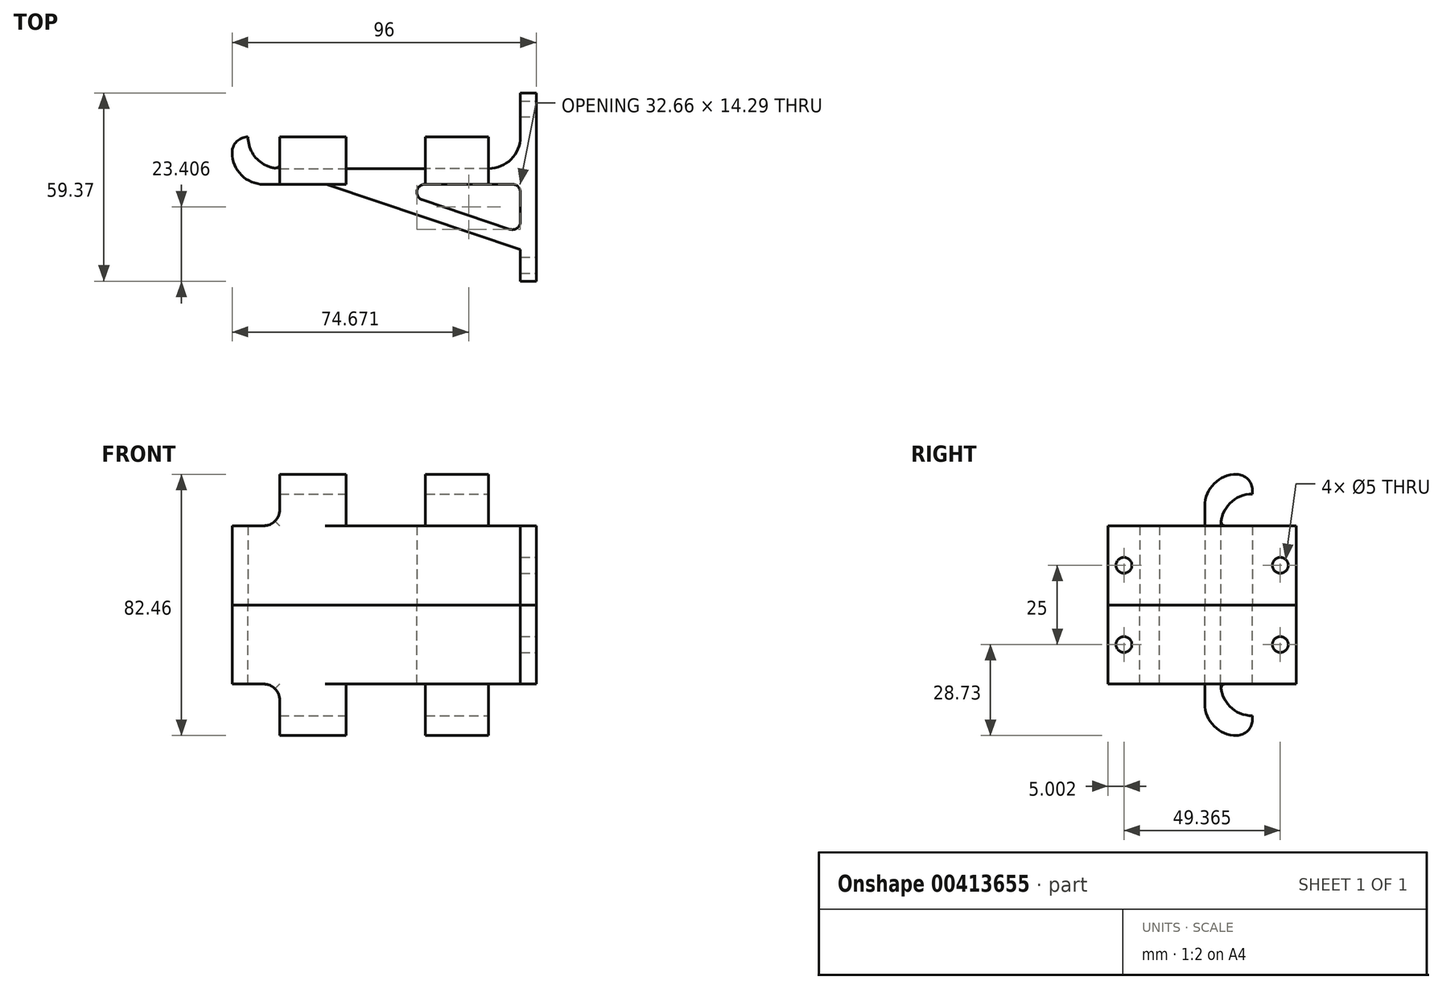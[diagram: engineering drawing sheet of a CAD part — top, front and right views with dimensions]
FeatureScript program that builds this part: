
annotation { "Feature Type Name" : "Feature", "Feature Type Description" : "" }
export const myFeature = defineFeature(function(context is Context, id is Id, definition is map)
    precondition{}
    {
        {
            var Q0;
            Q0=qCreatedBy(makeId("Top.planeOp"),FACE);
            var sketch = newSketch(context, id + "F0", { "sketchPlane" : qUnion([Q0])});
            skLineSegment(sketch, "E0", {"start": v(11.9, 15) * mm, "end": v(11.9, 15) * mm});
            skLineSegment(sketch, "E1", {"start": v(1.9, 5) * mm, "end": v(-64.1, 5) * mm});
            skLineSegment(sketch, "E2", {"start": v(-74.1, 15) * mm, "end": v(-74.1, 15) * mm});
            skLineSegment(sketch, "E3", {"start": v(-74.1, 15) * mm, "end": v(-79.1, 15) * mm});
            skLineSegment(sketch, "E4", {"start": v(-79.1, 15) * mm, "end": v(-79.1, 10) * mm});
            skLineSegment(sketch, "E5", {"start": v(-69.1, 0) * mm, "end": v(-49.3, 0) * mm});
            skLineSegment(sketch, "E6", {"start": v(11.9, 0) * mm, "end": v(11.9, -15.27) * mm});
            skLineSegment(sketch, "E7", {"start": v(11.9, -30.55) * mm, "end": v(16.9, -30.55) * mm});
            skLineSegment(sketch, "E8", {"start": v(16.9, -30.55) * mm, "end": v(16.9, 15) * mm});
            skLineSegment(sketch, "E9", {"start": v(-33.6, 0) * mm, "end": v(11.9, -15.27) * mm});
            skLineSegment(sketch, "E10", {"start": v(-49.3, 0) * mm, "end": v(11.9, -20.55) * mm});
            skLineSegment(sketch, "E11.trimOffspring", {"start": v(-33.6, 0) * mm, "end": v(11.9, 0) * mm});
            skLineSegment(sketch, "E12.trimOffspring", {"start": v(11.9, -20.55) * mm, "end": v(11.9, -30.55) * mm});
            skPoint(sketch, "E13.visualSharp", {"position": v(11.9, 5) * mm});
            skArc(sketch, "E13.filletArc", {"start": v(1.9, 5) * mm, "mid": v(8.97, 7.93) * mm, "end": v(11.9, 15) * mm});
            skPoint(sketch, "E14.visualSharp", {"position": v(-74.1, 5) * mm});
            skArc(sketch, "E14.filletArc", {"start": v(-74.1, 15) * mm, "mid": v(-71.17, 7.93) * mm, "end": v(-64.1, 5) * mm});
            skPoint(sketch, "E15.visualSharp", {"position": v(-79.1, 0) * mm});
            skArc(sketch, "E15.filletArc", {"start": v(-79.1, 10) * mm, "mid": v(-76.17, 2.93) * mm, "end": v(-69.1, 0) * mm});
            skLineSegment(sketch, "E16.right", {"start": v(16.9, 15) * mm, "end": v(16.9, 15) * mm});
            skLineSegment(sketch, "E17.top", {"start": v(11.9, 28.82) * mm, "end": v(16.9, 28.82) * mm});
            skLineSegment(sketch, "E17.left", {"start": v(11.9, 15) * mm, "end": v(11.9, 28.82) * mm});
            skLineSegment(sketch, "E17.right", {"start": v(16.9, 15) * mm, "end": v(16.9, 28.82) * mm});
            skSolve(sketch);
        }
        {
            var Q0;
            Q0=makeQuery(id+"F0.imprint","IMPRINT",FACE,{"disambiguationData":[TD([[makeQuery(id+"F0.imprint","IMPRINT",EDGE,{"derivedFrom":sQuery(id+"F0.wireOp",EDGE,"E1")}),1.0]])]});
            extrude(context, id + "F1", {"entities" : qUnion([Q0]), "depth" : 25 * mm});
        }
        {
            var Q0;
            Q0=makeQuery(id+"F1.opExtrude","SWEPT_FACE",FACE,{"disambiguationData":[OSD([sQuery(id+"F0.wireOp",EDGE,"E8"),sQuery(id+"F0.wireOp",EDGE,"E17.right")])]});
            var sketch = newSketch(context, id + "F2", { "sketchPlane" : qUnion([Q0])});
            skCircle(sketch, "E18", {"center": v(-25.55, 12.5) * mm, "radius": 2.5 * mm});
            skCircle(sketch, "E19", {"center": v(23.82, 12.5) * mm, "radius": 2.5 * mm});
            skSolve(sketch);
        }
        {
            var Q0;
            Q0 = qSketchRegion(id + "F2", true);
            extrude(context, id + "F3", {"entities" : qUnion([Q0]), "operationType" : NewBodyOperationType.REMOVE, "oppositeDirection" : true, "depth" : 25 * mm});
        }
        {
            var Q0;
            Q0=makeQuery(id+"F1.opExtrude","SWEPT_EDGE",EDGE,{"disambiguationData":[OSD([sQuery(id+"F0.wireOp",EDGE,"E3"),sQuery(id+"F0.wireOp",EDGE,"E4")])]});
            fillet(context, id + "F4", {"entities" : qUnion([Q0]), "radius" : 5 * mm, "tangentPropagation" : true, "allowEdgeOverflow" : false});
        }
        {
            var Q0;
            Q0=makeQuery(id+"F1.opExtrude","SWEPT_EDGE",EDGE,{"disambiguationData":[OSD([sQuery(id+"F0.wireOp",EDGE,"E9"),sQuery(id+"F0.wireOp",EDGE,"E11.trimOffspring")])]});
            var Q1;
            Q1=makeQuery(id+"F1.opExtrude","SWEPT_EDGE",EDGE,{"disambiguationData":[OSD([sQuery(id+"F0.wireOp",EDGE,"E6"),sQuery(id+"F0.wireOp",EDGE,"E11.trimOffspring")])]});
            var Q2;
            Q2=makeQuery(id+"F1.opExtrude","SWEPT_EDGE",EDGE,{"disambiguationData":[OSD([sQuery(id+"F0.wireOp",EDGE,"E6"),sQuery(id+"F0.wireOp",EDGE,"E9")])]});
            var Q3;
            Q3=makeQuery(id+"F1.opExtrude","SWEPT_EDGE",EDGE,{"disambiguationData":[OSD([sQuery(id+"F0.wireOp",EDGE,"E5"),sQuery(id+"F0.wireOp",EDGE,"E10")])]});
            fillet(context, id + "F5", {"entities" : qUnion([Q0, Q1, Q2, Q3]), "radius" : 2.5 * mm, "tangentPropagation" : true, "allowEdgeOverflow" : false});
        }
        {
            var Q0;
            Q0=makeQuery(id+"F1.opExtrude","SWEPT_FACE",FACE,{"disambiguationData":[OSD([sQuery(id+"F0.wireOp",EDGE,"E8"),sQuery(id+"F0.wireOp",EDGE,"E17.right")])]});
            var sketch = newSketch(context, id + "F6", { "sketchPlane" : qUnion([Q0])});
            skLineSegment(sketch, "E20", {"start": v(0, 25) * mm, "end": v(0, 31.23) * mm});
            skLineSegment(sketch, "E21", {"start": v(10, 41.23) * mm, "end": v(15, 41.23) * mm});
            skLineSegment(sketch, "E22", {"start": v(15, 41.23) * mm, "end": v(15, 35) * mm});
            skLineSegment(sketch, "E23", {"start": v(15, 35) * mm, "end": v(15, 35) * mm});
            skLineSegment(sketch, "E24", {"start": v(5, 25) * mm, "end": v(5, 25) * mm});
            skLineSegment(sketch, "E25", {"start": v(5, 25) * mm, "end": v(0, 25) * mm});
            skPoint(sketch, "E26.visualSharp", {"position": v(5, 35) * mm});
            skArc(sketch, "E26.filletArc", {"start": v(15, 35) * mm, "mid": v(7.93, 32.07) * mm, "end": v(5, 25) * mm});
            skPoint(sketch, "E27.visualSharp", {"position": v(0, 41.23) * mm});
            skArc(sketch, "E27.filletArc", {"start": v(10, 41.23) * mm, "mid": v(2.93, 38.3) * mm, "end": v(0, 31.23) * mm});
            skSolve(sketch);
        }
        {
            var Q0;
            Q0 = qSketchRegion(id + "F6", true);
            extrude(context, id + "F7", {"entities" : qUnion([Q0]), "operationType" : NewBodyOperationType.ADD, "oppositeDirection" : true, "depth" : 35 * mm, "hasSecondDirection" : true, "secondDirectionOppositeDirection" : true, "secondDirectionDepth" : 15 * mm});
        }
        {
            var Q0;
            Q0 = qSketchRegion(id + "F6", true);
            extrude(context, id + "F8", {"entities" : qUnion([Q0]), "operationType" : NewBodyOperationType.ADD, "oppositeDirection" : true, "depth" : 81 * mm, "hasSecondDirection" : true, "secondDirectionOppositeDirection" : true, "secondDirectionDepth" : 60 * mm});
        }
        {
            var Q0;
            Q0=makeQuery(id+"F8.opExtrude","SWEPT_EDGE",EDGE,{"disambiguationData":[OSD([sQuery(id+"F6.wireOp",EDGE,"E21"),sQuery(id+"F6.wireOp",EDGE,"E22")])]});
            fillet(context, id + "F9", {"entities" : qUnion([Q0]), "radius" : 5 * mm, "tangentPropagation" : true, "allowEdgeOverflow" : false});
        }
        {
            var Q0;
            Q0=makeQuery(id+"F7.opExtrude","SWEPT_EDGE",EDGE,{"disambiguationData":[OSD([sQuery(id+"F6.wireOp",EDGE,"E21"),sQuery(id+"F6.wireOp",EDGE,"E22")])]});
            var Q1;
            Q1=makeQuery(id+"F7.opExtrude","CAP_EDGE",EDGE,{"disambiguationData":[OSD([sQuery(id+"F6.wireOp",EDGE,"E25")])],"isStart":true});
            var Q2;
            Q2=makeQuery(id+"F8.opExtrude","CAP_EDGE",EDGE,{"disambiguationData":[OSD([sQuery(id+"F6.wireOp",EDGE,"E25")])],"isStart":false});
            var Q3;
            Q3=makeQuery(id+"F8.opExtrude","CAP_EDGE",EDGE,{"disambiguationData":[OSD([sQuery(id+"F6.wireOp",EDGE,"E25")])],"isStart":true});
            var Q4;
            Q4=makeQuery(id+"F7.opExtrude","CAP_EDGE",EDGE,{"disambiguationData":[OSD([sQuery(id+"F6.wireOp",EDGE,"E25")])],"isStart":false});
            fillet(context, id + "F10", {"entities" : qUnion([Q0, Q1, Q2, Q3, Q4]), "radius" : 5 * mm, "tangentPropagation" : true, "allowEdgeOverflow" : false});
        }
        {
            var Q0;
            Q0=makeQuery(id+"F1.opExtrude","SWEPT_BODY",BODY,{"disambiguationData":[OSD([sQuery(id+"F0.wireOp",EDGE,"E1"),sQuery(id+"F0.wireOp",EDGE,"E3"),sQuery(id+"F0.wireOp",EDGE,"E4"),sQuery(id+"F0.wireOp",EDGE,"E5"),sQuery(id+"F0.wireOp",EDGE,"E6"),sQuery(id+"F0.wireOp",EDGE,"E7"),sQuery(id+"F0.wireOp",EDGE,"E8"),sQuery(id+"F0.wireOp",EDGE,"E9"),sQuery(id+"F0.wireOp",EDGE,"E10"),sQuery(id+"F0.wireOp",EDGE,"E11.trimOffspring"),sQuery(id+"F0.wireOp",EDGE,"E12.trimOffspring"),sQuery(id+"F0.wireOp",EDGE,"E13.filletArc"),sQuery(id+"F0.wireOp",EDGE,"E14.filletArc"),sQuery(id+"F0.wireOp",EDGE,"E15.filletArc"),sQuery(id+"F0.wireOp",EDGE,"E17.top"),sQuery(id+"F0.wireOp",EDGE,"E17.left"),sQuery(id+"F0.wireOp",EDGE,"E17.right")])]});
            var Q1;
            Q1=qCreatedBy(makeId("Top.planeOp"),FACE);
            mirror(context, id + "F11", {"entities" : qUnion([Q0]), "mirrorPlane" : qUnion([Q1])});
        }
    });
